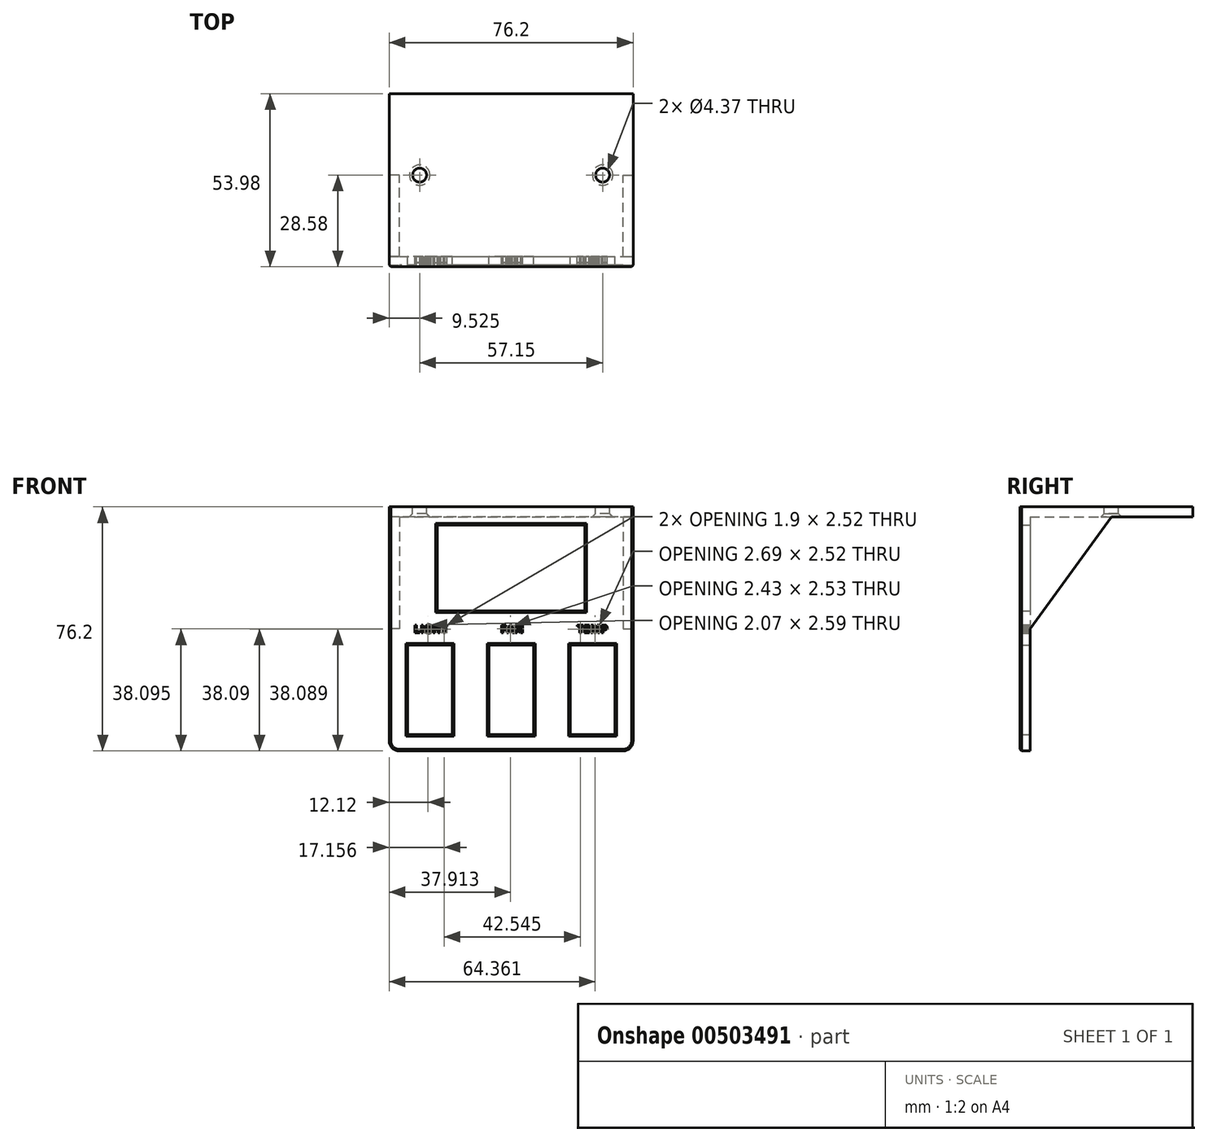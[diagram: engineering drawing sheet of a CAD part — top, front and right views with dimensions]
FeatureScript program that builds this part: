
annotation { "Feature Type Name" : "Feature", "Feature Type Description" : "" }
export const myFeature = defineFeature(function(context is Context, id is Id, definition is map)
    precondition{}
    {
        {
            var Q0;
            Q0=qCreatedBy(makeId("Front.planeOp"),FACE);
            var sketch = newSketch(context, id + "F0", { "sketchPlane" : qUnion([Q0])});
            skLineSegment(sketch, "E0.bottom", {"start": v(-38.1, 38.1) * mm, "end": v(38.1, 38.1) * mm});
            skLineSegment(sketch, "E0.top", {"start": v(-34.92, -38.1) * mm, "end": v(34.92, -38.1) * mm});
            skLineSegment(sketch, "E0.left", {"start": v(-38.1, 38.1) * mm, "end": v(-38.1, -34.93) * mm});
            skLineSegment(sketch, "E0.right", {"start": v(38.1, 38.1) * mm, "end": v(38.1, -34.93) * mm});
            skPoint(sketch, "E0.middle", {"position": v(0, 0) * mm});
            skLineSegment(sketch, "E1", {"start": v(0, 0) * mm, "end": v(0, 38.1) * mm, "construction": true});
            skLineSegment(sketch, "E2.bottom", {"start": v(-23.05, 32.45) * mm, "end": v(23.05, 32.45) * mm});
            skLineSegment(sketch, "E2.top", {"start": v(-23.05, 5.65) * mm, "end": v(23.05, 5.65) * mm});
            skLineSegment(sketch, "E2.left", {"start": v(-23.05, 32.45) * mm, "end": v(-23.05, 5.65) * mm});
            skLineSegment(sketch, "E2.right", {"start": v(23.05, 32.45) * mm, "end": v(23.05, 5.65) * mm});
            skPoint(sketch, "E2.middle", {"position": v(0, 19.05) * mm});
            skLineSegment(sketch, "E3", {"start": v(0, 0) * mm, "end": v(0, -38.1) * mm, "construction": true});
            skLineSegment(sketch, "E4.bottom", {"start": v(6.98, -33.02) * mm, "end": v(-6.99, -33.02) * mm});
            skLineSegment(sketch, "E4.top", {"start": v(6.98, -5.08) * mm, "end": v(-6.99, -5.08) * mm});
            skLineSegment(sketch, "E4.left", {"start": v(6.98, -33.02) * mm, "end": v(6.98, -5.08) * mm});
            skLineSegment(sketch, "E4.right", {"start": v(-6.99, -33.02) * mm, "end": v(-6.99, -5.08) * mm});
            skPoint(sketch, "E4.middle", {"position": v(0, -19.05) * mm});
            skLineSegment(sketch, "E5", {"start": v(-38.1, 0) * mm, "end": v(38.1, 0) * mm, "construction": true});
            skLineSegment(sketch, "E6", {"start": v(25.4, 0) * mm, "end": v(25.4, -38.1) * mm, "construction": true});
            skLineSegment(sketch, "E7.bottom", {"start": v(18.41, -5.08) * mm, "end": v(32.38, -5.08) * mm});
            skLineSegment(sketch, "E7.top", {"start": v(18.41, -33.02) * mm, "end": v(32.38, -33.02) * mm});
            skLineSegment(sketch, "E7.left", {"start": v(18.41, -5.08) * mm, "end": v(18.41, -33.02) * mm});
            skLineSegment(sketch, "E7.right", {"start": v(32.38, -5.08) * mm, "end": v(32.38, -33.02) * mm});
            skPoint(sketch, "E7.middle", {"position": v(25.4, -19.05) * mm});
            skLineSegment(sketch, "E8", {"start": v(-25.4, 0) * mm, "end": v(-25.4, -38.1) * mm, "construction": true});
            skLineSegment(sketch, "E9.bottom", {"start": v(-18.41, -33.02) * mm, "end": v(-32.39, -33.02) * mm});
            skLineSegment(sketch, "E9.top", {"start": v(-18.41, -5.08) * mm, "end": v(-32.39, -5.08) * mm});
            skLineSegment(sketch, "E9.left", {"start": v(-18.41, -33.02) * mm, "end": v(-18.41, -5.08) * mm});
            skLineSegment(sketch, "E9.right", {"start": v(-32.39, -33.02) * mm, "end": v(-32.39, -5.08) * mm});
            skPoint(sketch, "E9.middle", {"position": v(-25.4, -19.05) * mm});
            skPoint(sketch, "E10.visualSharp", {"position": v(-38.1, -38.1) * mm});
            skArc(sketch, "E10.filletArc", {"start": v(-38.1, -34.93) * mm, "mid": v(-37.17, -37.17) * mm, "end": v(-34.92, -38.1) * mm});
            skPoint(sketch, "E11.visualSharp", {"position": v(38.1, -38.1) * mm});
            skArc(sketch, "E11.filletArc", {"start": v(34.92, -38.1) * mm, "mid": v(37.17, -37.17) * mm, "end": v(38.1, -34.93) * mm});
            skLineSegment(sketch, "E12.bottom", {"start": v(-18.41, -3.18) * mm, "end": v(-32.39, -3.18) * mm, "construction": true});
            skLineSegment(sketch, "E12.top", {"start": v(-18.41, 3.17) * mm, "end": v(-32.39, 3.17) * mm, "construction": true});
            skLineSegment(sketch, "E12.left", {"start": v(-18.41, -3.18) * mm, "end": v(-18.41, 3.17) * mm, "construction": true});
            skLineSegment(sketch, "E12.right", {"start": v(-32.39, -3.18) * mm, "end": v(-32.39, 3.17) * mm, "construction": true});
            skPoint(sketch, "E12.middle", {"position": v(-25.4, 0) * mm});
            skLineSegment(sketch, "E13.bottom", {"start": v(6.98, -3.18) * mm, "end": v(-6.98, -3.18) * mm, "construction": true});
            skLineSegment(sketch, "E13.top", {"start": v(6.98, 3.18) * mm, "end": v(-6.98, 3.18) * mm, "construction": true});
            skLineSegment(sketch, "E13.left", {"start": v(6.98, -3.18) * mm, "end": v(6.98, 3.18) * mm, "construction": true});
            skLineSegment(sketch, "E13.right", {"start": v(-6.98, -3.18) * mm, "end": v(-6.98, 3.18) * mm, "construction": true});
            skLineSegment(sketch, "E14.bottom", {"start": v(32.07, -3.17) * mm, "end": v(18.73, -3.17) * mm, "construction": true});
            skLineSegment(sketch, "E14.top", {"start": v(32.07, 3.18) * mm, "end": v(18.73, 3.18) * mm, "construction": true});
            skLineSegment(sketch, "E14.left", {"start": v(32.07, -3.17) * mm, "end": v(32.07, 3.18) * mm, "construction": true});
            skLineSegment(sketch, "E14.right", {"start": v(18.73, -3.17) * mm, "end": v(18.73, 3.18) * mm, "construction": true});
            skPoint(sketch, "E14.middle", {"position": v(25.4, 0) * mm});
            skText(sketch, "E15", { "text": "LIGHT", "fontName": "OpenSans-Bold.ttf"});
            skText(sketch, "E16", { "text": "FAN", "fontName": "OpenSans-Bold.ttf"});
            skText(sketch, "E17", { "text": "TEMP", "fontName": "OpenSans-Bold.ttf"});
            const initialGuessF0  = {"E15": [-0.03038, -0.00127, 1, 0, 0.00254], "E16": [-0.00334, -0.00127, 1, 0, 0.00254], "E17": [0.02058, -0.00127, 1, 0, 0.00254]};
            skSetInitialGuess(sketch, initialGuessF0);
            skSolve(sketch);
        }
        {
            var Q0;
            Q0=makeQuery(id+"F0.imprint","IMPRINT",FACE,{"disambiguationData":[TD([[makeQuery(id+"F0.imprint","IMPRINT",EDGE,{"derivedFrom":sQuery(id+"F0.wireOp",EDGE,"E0.bottom")}),-1.0]])]});
            var Q1;
            Q1=makeQuery(id+"F0.imprint","IMPRINT",FACE,{"disambiguationData":[TD([[makeQuery(id+"F0.imprint","IMPRINT",EDGE,{"derivedFrom":sQuery(id+"F0.wireOp",EDGE,"E16.sketch_text.stroke-18")}),1.0]])]});
            var Q2;
            Q2=makeQuery(id+"F0.imprint","IMPRINT",FACE,{"disambiguationData":[TD([[makeQuery(id+"F0.imprint","IMPRINT",EDGE,{"derivedFrom":sQuery(id+"F0.wireOp",EDGE,"E17.sketch_text.stroke-39")}),1.0]])]});
            extrude(context, id + "F1", {"entities" : qUnion([Q0, Q1, Q2]), "depth" : 3.17 * mm});
        }
        {
            var Q0;
            Q0=makeQuery(id+"F0.imprint","IMPRINT",FACE,{"disambiguationData":[TD([[makeQuery(id+"F0.imprint","IMPRINT",EDGE,{"derivedFrom":sQuery(id+"F0.wireOp",EDGE,"E15.sketch_text.stroke-0")}),-1.0]])]});
            var Q1;
            Q1=makeQuery(id+"F0.imprint","IMPRINT",FACE,{"disambiguationData":[TD([[makeQuery(id+"F0.imprint","IMPRINT",EDGE,{"derivedFrom":sQuery(id+"F0.wireOp",EDGE,"E15.sketch_text.stroke-6")}),-1.0]])]});
            var Q2;
            Q2=makeQuery(id+"F0.imprint","IMPRINT",FACE,{"disambiguationData":[TD([[makeQuery(id+"F0.imprint","IMPRINT",EDGE,{"derivedFrom":sQuery(id+"F0.wireOp",EDGE,"E15.sketch_text.stroke-10")}),-1.0]])]});
            var Q3;
            Q3=makeQuery(id+"F0.imprint","IMPRINT",FACE,{"disambiguationData":[TD([[makeQuery(id+"F0.imprint","IMPRINT",EDGE,{"derivedFrom":sQuery(id+"F0.wireOp",EDGE,"E15.sketch_text.stroke-29")}),-1.0]])]});
            var Q4;
            Q4=makeQuery(id+"F0.imprint","IMPRINT",FACE,{"disambiguationData":[TD([[makeQuery(id+"F0.imprint","IMPRINT",EDGE,{"derivedFrom":sQuery(id+"F0.wireOp",EDGE,"E15.sketch_text.stroke-41")}),-1.0]])]});
            var Q5;
            Q5=makeQuery(id+"F0.imprint","IMPRINT",FACE,{"disambiguationData":[TD([[makeQuery(id+"F0.imprint","IMPRINT",EDGE,{"derivedFrom":sQuery(id+"F0.wireOp",EDGE,"E16.sketch_text.stroke-0")}),-1.0]])]});
            var Q6;
            Q6=makeQuery(id+"F0.imprint","IMPRINT",FACE,{"disambiguationData":[TD([[makeQuery(id+"F0.imprint","IMPRINT",EDGE,{"derivedFrom":sQuery(id+"F0.wireOp",EDGE,"E16.sketch_text.stroke-10")}),-1.0]])]});
            var Q7;
            Q7=makeQuery(id+"F0.imprint","IMPRINT",FACE,{"disambiguationData":[TD([[makeQuery(id+"F0.imprint","IMPRINT",EDGE,{"derivedFrom":sQuery(id+"F0.wireOp",EDGE,"E16.sketch_text.stroke-22")}),-1.0]])]});
            var Q8;
            Q8=makeQuery(id+"F0.imprint","IMPRINT",FACE,{"disambiguationData":[TD([[makeQuery(id+"F0.imprint","IMPRINT",EDGE,{"derivedFrom":sQuery(id+"F0.wireOp",EDGE,"E17.sketch_text.stroke-0")}),-1.0]])]});
            var Q9;
            Q9=makeQuery(id+"F0.imprint","IMPRINT",FACE,{"disambiguationData":[TD([[makeQuery(id+"F0.imprint","IMPRINT",EDGE,{"derivedFrom":sQuery(id+"F0.wireOp",EDGE,"E17.sketch_text.stroke-8")}),-1.0]])]});
            var Q10;
            Q10=makeQuery(id+"F0.imprint","IMPRINT",FACE,{"disambiguationData":[TD([[makeQuery(id+"F0.imprint","IMPRINT",EDGE,{"derivedFrom":sQuery(id+"F0.wireOp",EDGE,"E17.sketch_text.stroke-20")}),-1.0]])]});
            var Q11;
            Q11=makeQuery(id+"F0.imprint","IMPRINT",FACE,{"disambiguationData":[TD([[makeQuery(id+"F0.imprint","IMPRINT",EDGE,{"derivedFrom":sQuery(id+"F0.wireOp",EDGE,"E17.sketch_text.stroke-39")}),-1.0]])]});
            extrude(context, id + "F2", {"entities" : qUnion([Q0, Q1, Q2, Q3, Q4, Q5, Q6, Q7, Q8, Q9, Q10, Q11]), "depth" : 1.9 * mm});
        }
        {
            var Q0;
            Q0=makeQuery(id+"F1.opExtrude","SWEPT_FACE",FACE,{"disambiguationData":[OSD([sQuery(id+"F0.wireOp",EDGE,"E0.bottom")])]});
            var sketch = newSketch(context, id + "F3", { "sketchPlane" : qUnion([Q0])});
            skLineSegment(sketch, "E18.bottom", {"start": v(38.1, 0) * mm, "end": v(-38.1, 0) * mm});
            skLineSegment(sketch, "E18.top", {"start": v(38.1, 50.8) * mm, "end": v(-38.1, 50.8) * mm});
            skLineSegment(sketch, "E18.left", {"start": v(38.1, 0) * mm, "end": v(38.1, 50.8) * mm});
            skLineSegment(sketch, "E18.right", {"start": v(-38.1, 0) * mm, "end": v(-38.1, 50.8) * mm});
            skLineSegment(sketch, "E19", {"start": v(0, 0) * mm, "end": v(0, 50.8) * mm, "construction": true});
            skLineSegment(sketch, "E20", {"start": v(-38.1, 25.4) * mm, "end": v(38.1, 25.4) * mm, "construction": true});
            skCircle(sketch, "E21", {"center": v(28.57, 25.4) * mm, "radius": 2.18 * mm});
            skCircle(sketch, "E22.MirrorC", {"center": v(-28.57, 25.4) * mm, "radius": 2.18 * mm});
            skSolve(sketch);
        }
        {
            var Q0;
            Q0=makeQuery(id+"F3.imprint","IMPRINT",FACE,{"disambiguationData":[TD([[makeQuery(id+"F3.imprint","IMPRINT",EDGE,{"derivedFrom":sQuery(id+"F3.wireOp",EDGE,"E18.bottom")}),1.0]])]});
            extrude(context, id + "F4", {"entities" : qUnion([Q0]), "operationType" : NewBodyOperationType.ADD, "oppositeDirection" : true, "depth" : 3.17 * mm});
        }
        {
            var Q0;
            Q0=makeQuery(id+"F4.opExtrude","CAP_EDGE",EDGE,{"disambiguationData":[OSD([sQuery(id+"F3.wireOp",EDGE,"E22.MirrorC")])],"isStart":false});
            var Q1;
            Q1=makeQuery(id+"F4.opExtrude","CAP_EDGE",EDGE,{"disambiguationData":[OSD([sQuery(id+"F3.wireOp",EDGE,"E21")])],"isStart":false});
            chamfer(context, id + "F5", {"entities" : qUnion([Q0, Q1]), "width" : 1.02 * mm, "tangentPropagation" : true});
        }
        {
            var Q0;
            Q0=makeQuery(id+"F4.boolean.opBoolean","MERGE",FACE,{"derivedFrom":[makeQuery(id+"F1.opExtrude","SWEPT_FACE",FACE,{"disambiguationData":[OSD([sQuery(id+"F0.wireOp",EDGE,"E0.right")])]}),makeQuery(id+"F4.opExtrude","SWEPT_FACE",FACE,{"disambiguationData":[OSD([sQuery(id+"F3.wireOp",EDGE,"E18.left")])]})]});
            var sketch = newSketch(context, id + "F6", { "sketchPlane" : qUnion([Q0])});
            skLineSegment(sketch, "E23", {"start": v(0, 0) * mm, "end": v(25.4, 34.93) * mm});
            skSolve(sketch);
        }
        {
            var Q0;
            {var subQ0=sQuery(id+"F6.wireOp",EDGE,"E23");Q0=makeQuery(id+"F6.imprint","IMPRINT",FACE,{"disambiguationData":[TD([[makeQuery(id+"F6.imprint","IMPRINT",EDGE,{"derivedFrom":subQ0}),1.0]])]});}
            extrude(context, id + "F7", {"entities" : qUnion([Q0]), "operationType" : NewBodyOperationType.ADD, "oppositeDirection" : true, "depth" : 3.17 * mm});
        }
        {
            var Q0;
            Q0=makeQuery(id+"F4.boolean.opBoolean","MERGE",FACE,{"derivedFrom":[makeQuery(id+"F1.opExtrude","SWEPT_FACE",FACE,{"disambiguationData":[OSD([sQuery(id+"F0.wireOp",EDGE,"E0.left")])]}),makeQuery(id+"F4.opExtrude","SWEPT_FACE",FACE,{"disambiguationData":[OSD([sQuery(id+"F3.wireOp",EDGE,"E18.right")])]})]});
            var sketch = newSketch(context, id + "F8", { "sketchPlane" : qUnion([Q0])});
            skLineSegment(sketch, "E24", {"start": v(0, 0) * mm, "end": v(-25.4, 34.92) * mm});
            skSolve(sketch);
        }
        {
            var Q0;
            {var subQ0=sQuery(id+"F8.wireOp",EDGE,"E24");Q0=makeQuery(id+"F8.imprint","IMPRINT",FACE,{"disambiguationData":[TD([[makeQuery(id+"F8.imprint","IMPRINT",EDGE,{"derivedFrom":subQ0}),-1.0]])]});}
            extrude(context, id + "F9", {"entities" : qUnion([Q0]), "operationType" : NewBodyOperationType.ADD, "oppositeDirection" : true, "depth" : 3.17 * mm});
        }
        {
            var Q0;
            Q0=makeQuery(id+"F1.opExtrude","CAP_EDGE",EDGE,{"disambiguationData":[OSD([sQuery(id+"F0.wireOp",EDGE,"E2.left")])],"isStart":false});
            var Q1;
            Q1=makeQuery(id+"F1.opExtrude","CAP_EDGE",EDGE,{"disambiguationData":[OSD([sQuery(id+"F0.wireOp",EDGE,"E2.top")])],"isStart":false});
            var Q2;
            Q2=makeQuery(id+"F1.opExtrude","CAP_EDGE",EDGE,{"disambiguationData":[OSD([sQuery(id+"F0.wireOp",EDGE,"E2.right")])],"isStart":false});
            var Q3;
            Q3=makeQuery(id+"F1.opExtrude","CAP_EDGE",EDGE,{"disambiguationData":[OSD([sQuery(id+"F0.wireOp",EDGE,"E2.bottom")])],"isStart":false});
            var Q4;
            Q4=makeQuery(id+"F1.opExtrude","CAP_EDGE",EDGE,{"disambiguationData":[OSD([sQuery(id+"F0.wireOp",EDGE,"E7.right")])],"isStart":false});
            var Q5;
            Q5=makeQuery(id+"F1.opExtrude","CAP_EDGE",EDGE,{"disambiguationData":[OSD([sQuery(id+"F0.wireOp",EDGE,"E7.bottom")])],"isStart":false});
            var Q6;
            Q6=makeQuery(id+"F1.opExtrude","CAP_EDGE",EDGE,{"disambiguationData":[OSD([sQuery(id+"F0.wireOp",EDGE,"E7.left")])],"isStart":false});
            var Q7;
            Q7=makeQuery(id+"F1.opExtrude","CAP_EDGE",EDGE,{"disambiguationData":[OSD([sQuery(id+"F0.wireOp",EDGE,"E7.top")])],"isStart":false});
            var Q8;
            Q8=makeQuery(id+"F1.opExtrude","CAP_EDGE",EDGE,{"disambiguationData":[OSD([sQuery(id+"F0.wireOp",EDGE,"E4.left")])],"isStart":false});
            var Q9;
            Q9=makeQuery(id+"F1.opExtrude","CAP_EDGE",EDGE,{"disambiguationData":[OSD([sQuery(id+"F0.wireOp",EDGE,"E4.top")])],"isStart":false});
            var Q10;
            Q10=makeQuery(id+"F1.opExtrude","CAP_EDGE",EDGE,{"disambiguationData":[OSD([sQuery(id+"F0.wireOp",EDGE,"E4.right")])],"isStart":false});
            var Q11;
            Q11=makeQuery(id+"F1.opExtrude","CAP_EDGE",EDGE,{"disambiguationData":[OSD([sQuery(id+"F0.wireOp",EDGE,"E4.bottom")])],"isStart":false});
            var Q12;
            Q12=makeQuery(id+"F1.opExtrude","CAP_EDGE",EDGE,{"disambiguationData":[OSD([sQuery(id+"F0.wireOp",EDGE,"E9.bottom")])],"isStart":false});
            var Q13;
            Q13=makeQuery(id+"F1.opExtrude","CAP_EDGE",EDGE,{"disambiguationData":[OSD([sQuery(id+"F0.wireOp",EDGE,"E9.right")])],"isStart":false});
            var Q14;
            Q14=makeQuery(id+"F1.opExtrude","CAP_EDGE",EDGE,{"disambiguationData":[OSD([sQuery(id+"F0.wireOp",EDGE,"E9.top")])],"isStart":false});
            var Q15;
            Q15=makeQuery(id+"F1.opExtrude","CAP_EDGE",EDGE,{"disambiguationData":[OSD([sQuery(id+"F0.wireOp",EDGE,"E9.left")])],"isStart":false});
            var Q16;
            Q16=makeQuery(id+"F1.opExtrude","CAP_EDGE",EDGE,{"disambiguationData":[OSD([sQuery(id+"F0.wireOp",EDGE,"E0.right")])],"isStart":false});
            var Q17;
            Q17=makeQuery(id+"F1.opExtrude","CAP_EDGE",EDGE,{"disambiguationData":[OSD([sQuery(id+"F0.wireOp",EDGE,"E11.filletArc")])],"isStart":false});
            var Q18;
            Q18=makeQuery(id+"F1.opExtrude","CAP_EDGE",EDGE,{"disambiguationData":[OSD([sQuery(id+"F0.wireOp",EDGE,"E0.top")])],"isStart":false});
            var Q19;
            Q19=makeQuery(id+"F1.opExtrude","CAP_EDGE",EDGE,{"disambiguationData":[OSD([sQuery(id+"F0.wireOp",EDGE,"E10.filletArc")])],"isStart":false});
            var Q20;
            Q20=makeQuery(id+"F1.opExtrude","CAP_EDGE",EDGE,{"disambiguationData":[OSD([sQuery(id+"F0.wireOp",EDGE,"E0.left")])],"isStart":false});
            chamfer(context, id + "F10", {"entities" : qUnion([Q0, Q1, Q2, Q3, Q4, Q5, Q6, Q7, Q8, Q9, Q10, Q11, Q12, Q13, Q14, Q15, Q16, Q17, Q18, Q19, Q20]), "width" : 0.5 * mm, "tangentPropagation" : true});
        }
    });
